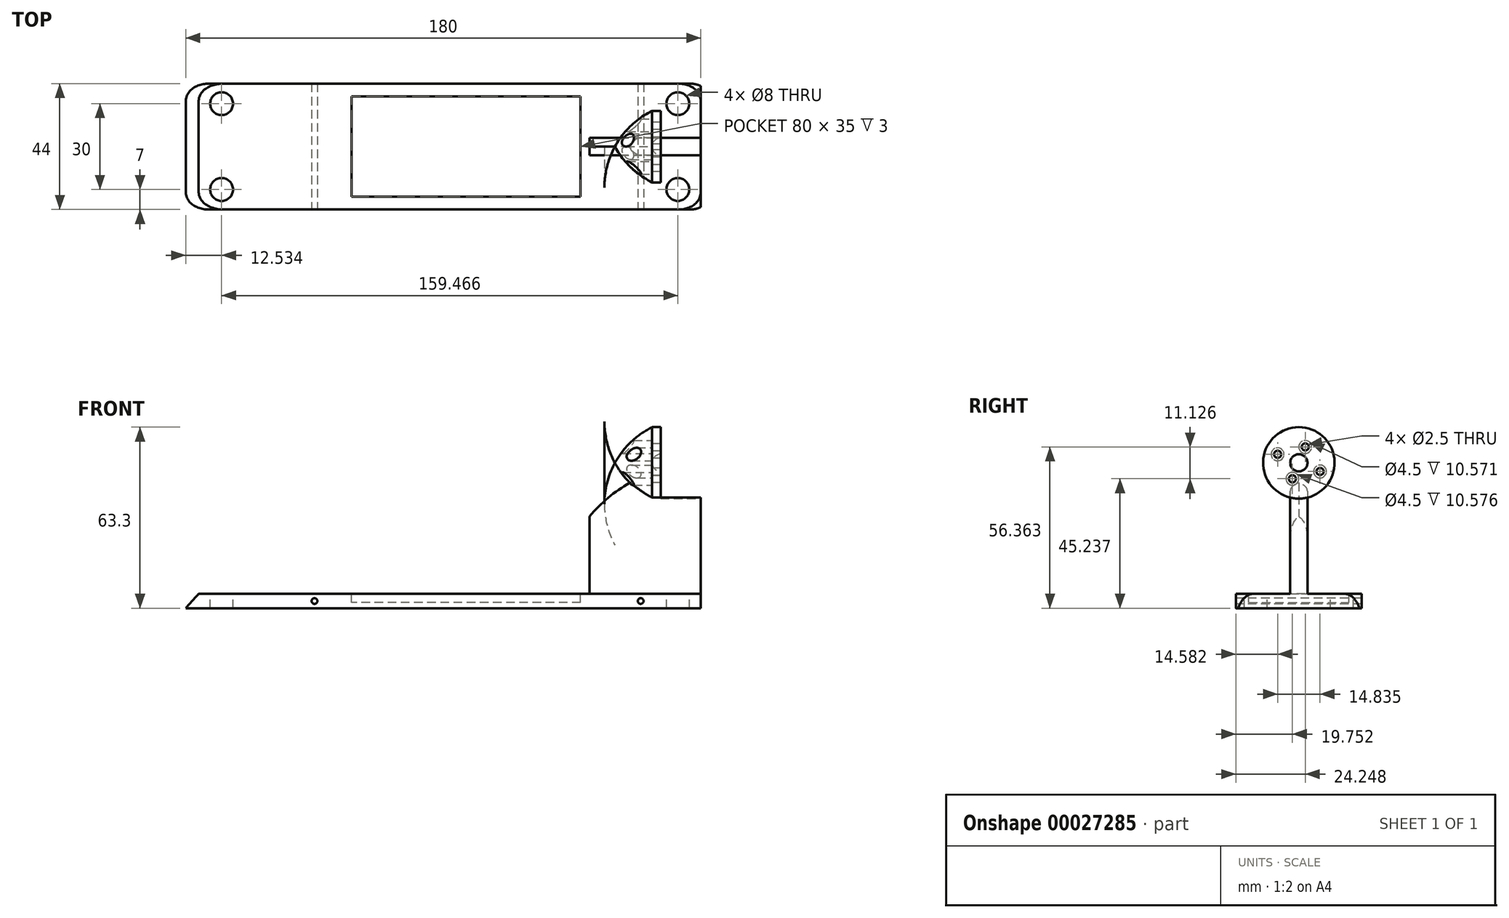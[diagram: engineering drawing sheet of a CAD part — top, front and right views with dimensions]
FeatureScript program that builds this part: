
annotation { "Feature Type Name" : "Feature", "Feature Type Description" : "" }
export const myFeature = defineFeature(function(context is Context, id is Id, definition is map)
    precondition{}
    {
        {
            var Q0;
            Q0=qCreatedBy(makeId("Top.planeOp"),FACE);
            var sketch = newSketch(context, id + "F0", { "sketchPlane" : qUnion([Q0])});
            skLineSegment(sketch, "E0.bottom", {"start": v(90, 22) * mm, "end": v(-90, 22) * mm});
            skLineSegment(sketch, "E0.top", {"start": v(90, -22) * mm, "end": v(-90, -22) * mm});
            skLineSegment(sketch, "E0.left", {"start": v(90, 22) * mm, "end": v(90, -22) * mm});
            skLineSegment(sketch, "E0.right", {"start": v(-90, 22) * mm, "end": v(-90, -22) * mm});
            skPoint(sketch, "E0.middle", {"position": v(0, 0) * mm});
            skSolve(sketch);
        }
        {
            var Q0;
            Q0 = qSketchRegion(id + "F0", true);
            extrude(context, id + "F1", {"entities" : qUnion([Q0]), "depth" : 37 * mm});
        }
        {
            var Q0;
            Q0=makeQuery(id+"F1.opExtrude","SWEPT_FACE",FACE,{"disambiguationData":[OSD([sQuery(id+"F0.wireOp",EDGE,"E0.left")])]});
            var sketch = newSketch(context, id + "F2", { "sketchPlane" : qUnion([Q0])});
            skLineSegment(sketch, "E1", {"start": v(0, 0) * mm, "end": v(0, 50.8) * mm});
            skCircle(sketch, "E2", {"center": v(0, 50.8) * mm, "radius": 11.5 * mm});
            skCircle(sketch, "E3", {"center": v(0, 50.8) * mm, "radius": 50.8 * mm, "construction": true});
            skSolve(sketch);
        }
        {
            var Q0;
            Q0=qCreatedBy(makeId("Front.planeOp"),FACE);
            var sketch = newSketch(context, id + "F3", { "sketchPlane" : qUnion([Q0])});
            skLineSegment(sketch, "E4.0", {"start": v(90, 0) * mm, "end": v(90, 50.8) * mm});
            skLineSegment(sketch, "E5.0", {"start": v(-90, 37) * mm, "end": v(-90, 0) * mm});
            skLineSegment(sketch, "E6.0", {"start": v(90, 37) * mm, "end": v(-90, 37) * mm});
            skArc(sketch, "E7", {"start": v(-10, 37) * mm, "mid": v(-54.07, 27.3) * mm, "end": v(-90, 0) * mm});
            skLineSegment(sketch, "E8", {"start": v(0, 37) * mm, "end": v(0, 0) * mm, "construction": true});
            skArc(sketch, "E9", {"start": v(90, 5) * mm, "mid": v(61.22, 28.57) * mm, "end": v(25, 37) * mm});
            skSolve(sketch);
        }
        {
            var Q0;
            Q0 = qSketchRegion(id + "F3", true);
            extrude(context, id + "F4", {"entities" : qUnion([Q0]), "operationType" : NewBodyOperationType.REMOVE, "oppositeDirection" : true, "depth" : 25 * mm, "hasSecondDirection" : true, "secondDirectionOppositeDirection" : false, "secondDirectionDepth" : 25 * mm});
        }
        {
            var Q0;
            Q0=qCreatedBy(makeId("Front.planeOp"),FACE);
            var sketch = newSketch(context, id + "F5", { "sketchPlane" : qUnion([Q0])});
            skLineSegment(sketch, "E10.top", {"start": v(48, 32) * mm, "end": v(-32, 32) * mm});
            skLineSegment(sketch, "E10.right", {"start": v(-32, 2) * mm, "end": v(-32, 32) * mm});
            skLineSegment(sketch, "E11", {"start": v(48, 32) * mm, "end": v(48, 2) * mm});
            skLineSegment(sketch, "E12", {"start": v(48, 2) * mm, "end": v(-32, 2) * mm});
            skSolve(sketch);
        }
        {
            var Q0;
            Q0 = qSketchRegion(id + "F5", true);
            extrude(context, id + "F6", {"entities" : qUnion([Q0]), "depth" : (35 / 2) * mm, "hasSecondDirection" : true, "secondDirectionOppositeDirection" : true, "secondDirectionDepth" : 17.5 * mm});
        }
        {
            var Q0;
            Q0=makeQuery(id+"F4.boolean.opBoolean","INTERSECT",EDGE,{"derivedFrom":[makeQuery(id+"F1.opExtrude","SWEPT_FACE",FACE,{"disambiguationData":[OSD([sQuery(id+"F0.wireOp",EDGE,"E0.bottom")])]}),makeQuery(id+"F4.opExtrude","SWEPT_FACE",FACE,{"disambiguationData":[OSD([sQuery(id+"F3.wireOp",EDGE,"E7")])]})]});
            var Q1;
            Q1=makeQuery(id+"F1.opExtrude","CAP_EDGE",EDGE,{"disambiguationData":[OSD([sQuery(id+"F0.wireOp",EDGE,"E0.bottom")])],"isStart":false});
            var Q2;
            Q2=makeQuery(id+"F4.boolean.opBoolean","INTERSECT",EDGE,{"derivedFrom":[makeQuery(id+"F1.opExtrude","SWEPT_FACE",FACE,{"disambiguationData":[OSD([sQuery(id+"F0.wireOp",EDGE,"E0.top")])]}),makeQuery(id+"F4.opExtrude","SWEPT_FACE",FACE,{"disambiguationData":[OSD([sQuery(id+"F3.wireOp",EDGE,"E7")])]})]});
            var Q3;
            Q3=makeQuery(id+"F4.boolean.opBoolean","INTERSECT",EDGE,{"derivedFrom":[makeQuery(id+"F1.opExtrude","SWEPT_FACE",FACE,{"disambiguationData":[OSD([sQuery(id+"F0.wireOp",EDGE,"E0.bottom")])]}),makeQuery(id+"F4.opExtrude","SWEPT_FACE",FACE,{"disambiguationData":[OSD([sQuery(id+"F3.wireOp",EDGE,"E9")])]})]});
            fillet(context, id + "F7", {"entities" : qUnion([Q0, Q1, Q2, Q3]), "radius" : 6 * mm, "tangentPropagation" : true, "allowEdgeOverflow" : false});
        }
        {
            var Q0;
            {var subQ1=sQuery(id+"F0.wireOp",EDGE,"E0.left");var subQ6=makeQuery(id+"F1.opExtrude","SWEPT_EDGE",EDGE,{"disambiguationData":[OSD([sQuery(id+"F0.wireOp",EDGE,"E0.top"),subQ1])]});Q0=makeQuery(id+"F2.imprint","IMPRINT",FACE,{"disambiguationData":[TD([[makeQuery(id+"F2.imprint","IMPRINT",EDGE,{"derivedFrom":subQ6}),1.0]])]});}
            var sketch = newSketch(context, id + "F8", { "sketchPlane" : qUnion([Q0])});
            skLineSegment(sketch, "E13.bottom", {"start": v(-3, 50.8) * mm, "end": v(3, 50.8) * mm});
            skLineSegment(sketch, "E13.top", {"start": v(-3, 0) * mm, "end": v(3, 0) * mm});
            skLineSegment(sketch, "E13.left", {"start": v(-3, 50.8) * mm, "end": v(-3, 0) * mm});
            skLineSegment(sketch, "E13.right", {"start": v(3, 50.8) * mm, "end": v(3, 0) * mm});
            skPoint(sketch, "E13.middle", {"position": v(0, 25.4) * mm});
            skLineSegment(sketch, "E14.0", {"start": v(0, 0) * mm, "end": v(0, 50.8) * mm, "construction": true});
            skSolve(sketch);
        }
        {
            var Q0;
            Q0 = qSketchRegion(id + "F8", true);
            var Q1;
            Q1=sQuery(id+"F8.wireOp",EDGE,"E13.top");
            revolve(context, id + "F9", {"operationType" : NewBodyOperationType.ADD, "entities" : qUnion([Q0]), "axis" : qUnion([Q1]), "revolveType" : RevolveType.ONE_DIRECTION, "oppositeDirection" : true, "angle" : 56 * degree});
        }
        {
            var Q0;
            Q0=makeQuery(id+"F2.imprint","IMPRINT",FACE,{"disambiguationData":[TD([[makeQuery(id+"F2.imprint","IMPRINT",EDGE,{"derivedFrom":sQuery(id+"F2.wireOp",EDGE,"E2")}),1.0]])]});
            var sketch = newSketch(context, id + "F10", { "sketchPlane" : qUnion([Q0])});
            skCircle(sketch, "E15.0", {"center": v(0, 50.8) * mm, "radius": 11.5 * mm, "construction": true});
            skCircle(sketch, "E16.0", {"center": v(0, 50.8) * mm, "radius": 12.5 * mm});
            skSolve(sketch);
        }
        {
            var Q0;
            Q0 = qSketchRegion(id + "F10", true);
            extrude(context, id + "F11", {"entities" : qUnion([Q0]), "operationType" : NewBodyOperationType.REMOVE, "oppositeDirection" : true, "depth" : 14 * mm});
        }
        {
            var Q0;
            Q0=qCreatedBy(makeId("Front.planeOp"),FACE);
            var sketch = newSketch(context, id + "F12", { "sketchPlane" : qUnion([Q0])});
            skPoint(sketch, "E17.0", {"position": v(90, 50.8) * mm});
            skLineSegment(sketch, "E18", {"start": v(90, 50.8) * mm, "end": v(60, 50.8) * mm});
            skLineSegment(sketch, "E19", {"start": v(73, 50.8) * mm, "end": v(73, 38.3) * mm, "construction": true});
            skArc(sketch, "E20", {"start": v(60, 50.8) * mm, "mid": v(65.54, 43.55) * mm, "end": v(73, 38.3) * mm});
            skLineSegment(sketch, "E21.0", {"start": v(76, 38.3) * mm, "end": v(76, 50.8) * mm});
            skPoint(sketch, "E22.orphan", {"position": v(76, 48.83) * mm});
            skLineSegment(sketch, "E23", {"start": v(73, 38.3) * mm, "end": v(76, 38.3) * mm});
            skPoint(sketch, "E24.orphan", {"position": v(76, 38.67) * mm});
            skSolve(sketch);
        }
        {
            var Q0;
            Q0 = qSketchRegion(id + "F12", true);
            var Q1;
            Q1=sQuery(id+"F12.wireOp",EDGE,"E18");
            revolve(context, id + "F13", {"operationType" : NewBodyOperationType.ADD, "entities" : qUnion([Q0]), "axis" : qUnion([Q1]), "revolveType" : RevolveType.FULL});
        }
        {
            var Q0;
            Q0=makeQuery(id+"F13.boolean.opBoolean","MERGE",FACE,{"derivedFrom":[makeQuery(id+"F11.boolean.opBoolean","COPY",FACE,{"derivedFrom":makeQuery(id+"F11.opExtrude","CAP_FACE",FACE,{"disambiguationData":[OSD([sQuery(id+"F10.wireOp",EDGE,"E16.0")])],"isStart":false})}),makeQuery(id+"F13.opRevolve","SWEPT_FACE",FACE,{"disambiguationData":[OSD([sQuery(id+"F12.wireOp",EDGE,"E21.0")])]})]});
            var sketch = newSketch(context, id + "F14", { "sketchPlane" : qUnion([Q0])});
            skLineSegment(sketch, "E25", {"start": v(7.42, 47.8) * mm, "end": v(-7.42, 53.8) * mm, "construction": true});
            skLineSegment(sketch, "E26", {"start": v(2.25, 56.36) * mm, "end": v(-2.25, 45.24) * mm, "construction": true});
            skCircle(sketch, "E27", {"center": v(-7.42, 53.8) * mm, "radius": 1.25 * mm});
            skCircle(sketch, "E28", {"center": v(2.25, 56.36) * mm, "radius": 1.25 * mm});
            skCircle(sketch, "E29", {"center": v(-2.25, 45.24) * mm, "radius": 1.25 * mm});
            skCircle(sketch, "E30", {"center": v(7.42, 47.8) * mm, "radius": 1.25 * mm});
            skSolve(sketch);
        }
        {
            var Q0;
            Q0 = qSketchRegion(id + "F14", true);
            extrude(context, id + "F15", {"entities" : qUnion([Q0]), "operationType" : NewBodyOperationType.REMOVE, "endBound" : BoundingType.THROUGH_ALL, "oppositeDirection" : true, "depth" : 25 * mm});
        }
        {
            var Q0;
            Q0=makeQuery(id+"F13.boolean.opBoolean","MERGE",FACE,{"derivedFrom":[makeQuery(id+"F11.boolean.opBoolean","COPY",FACE,{"derivedFrom":makeQuery(id+"F11.opExtrude","CAP_FACE",FACE,{"disambiguationData":[OSD([sQuery(id+"F10.wireOp",EDGE,"E16.0")])],"isStart":false})}),makeQuery(id+"F13.opRevolve","SWEPT_FACE",FACE,{"disambiguationData":[OSD([sQuery(id+"F12.wireOp",EDGE,"E21.0")])]})]});
            var sketch = newSketch(context, id + "F16", { "sketchPlane" : qUnion([Q0])});
            skCircle(sketch, "E31", {"center": v(0, 50.8) * mm, "radius": 3 * mm});
            skSolve(sketch);
        }
        {
            var Q0;
            Q0 = qSketchRegion(id + "F16", true);
            extrude(context, id + "F17", {"entities" : qUnion([Q0]), "operationType" : NewBodyOperationType.REMOVE, "oppositeDirection" : true, "depth" : 3 * mm});
        }
        {
            var Q0;
            Q0=makeQuery(id+"F17.boolean.opBoolean","COPY",EDGE,{"derivedFrom":makeQuery(id+"F17.opExtrude","CAP_EDGE",EDGE,{"disambiguationData":[OSD([sQuery(id+"F16.wireOp",EDGE,"E31")])],"isStart":false})});
            fillet(context, id + "F18", {"entities" : qUnion([Q0]), "radius" : 3 * mm, "tangentPropagation" : true, "allowEdgeOverflow" : false});
        }
        {
            var Q0;
            Q0=makeQuery(id+"F13.boolean.opBoolean","MERGE",FACE,{"derivedFrom":[makeQuery(id+"F11.boolean.opBoolean","COPY",FACE,{"derivedFrom":makeQuery(id+"F11.opExtrude","CAP_FACE",FACE,{"disambiguationData":[OSD([sQuery(id+"F10.wireOp",EDGE,"E16.0")])],"isStart":false})}),makeQuery(id+"F13.opRevolve","SWEPT_FACE",FACE,{"disambiguationData":[OSD([sQuery(id+"F12.wireOp",EDGE,"E21.0")])]})]});
            var sketch = newSketch(context, id + "F19", { "sketchPlane" : qUnion([Q0])});
            skCircle(sketch, "E32", {"center": v(-7.42, 53.8) * mm, "radius": 2.25 * mm});
            skCircle(sketch, "E33", {"center": v(2.25, 56.36) * mm, "radius": 2.25 * mm});
            skCircle(sketch, "E34", {"center": v(7.42, 47.8) * mm, "radius": 2.25 * mm});
            skCircle(sketch, "E35", {"center": v(-2.25, 45.24) * mm, "radius": 2.25 * mm});
            skSolve(sketch);
        }
        {
            var Q0;
            Q0 = qSketchRegion(id + "F19", true);
            extrude(context, id + "F20", {"entities" : qUnion([Q0]), "operationType" : NewBodyOperationType.REMOVE, "endBound" : BoundingType.THROUGH_ALL, "oppositeDirection" : true, "depth" : 6.3 * mm, "hasSecondDirection" : true, "secondDirectionOppositeDirection" : true, "secondDirectionDepth" : 3 * mm});
        }
        {
            var Q0;
            {var subQ1=sQuery(id+"F0.wireOp",EDGE,"E0.left");var subQ6=makeQuery(id+"F1.opExtrude","SWEPT_EDGE",EDGE,{"disambiguationData":[OSD([sQuery(id+"F0.wireOp",EDGE,"E0.bottom"),subQ1])]});Q0=makeQuery(id+"F2.imprint","IMPRINT",FACE,{"disambiguationData":[TD([[makeQuery(id+"F2.imprint","IMPRINT",EDGE,{"derivedFrom":subQ6}),-1.0]])]});}
            var sketch = newSketch(context, id + "F21", { "sketchPlane" : qUnion([Q0])});
            skLineSegment(sketch, "E36", {"start": v(-28, 5) * mm, "end": v(-3, 5) * mm});
            skLineSegment(sketch, "E37.0", {"start": v(-3, 38.67) * mm, "end": v(-3, 5) * mm});
            skLineSegment(sketch, "E37.1", {"start": v(3, 38.67) * mm, "end": v(3, 5) * mm});
            skLineSegment(sketch, "E38.trimOffspring", {"start": v(3, 5) * mm, "end": v(28, 5) * mm});
            skLineSegment(sketch, "E39", {"start": v(-28, 5) * mm, "end": v(-28, 38.67) * mm});
            skLineSegment(sketch, "E40", {"start": v(-28, 38.67) * mm, "end": v(-3, 38.67) * mm});
            skLineSegment(sketch, "E41", {"start": v(28, 5) * mm, "end": v(28, 38.67) * mm});
            skLineSegment(sketch, "E42", {"start": v(28, 38.67) * mm, "end": v(3, 38.67) * mm});
            skSolve(sketch);
        }
        {
            var Q0;
            Q0 = qSketchRegion(id + "F21", true);
            extrude(context, id + "F22", {"entities" : qUnion([Q0]), "operationType" : NewBodyOperationType.REMOVE, "endBound" : BoundingType.THROUGH_ALL, "oppositeDirection" : true, "depth" : 25 * mm});
        }
        {
            var Q0;
            Q0=makeQuery(id+"F22.boolean.opBoolean","MERGE",FACE,{"derivedFrom":[makeQuery(id+"F9.opRevolve","SWEPT_FACE",FACE,{"disambiguationData":[OSD([sQuery(id+"F8.wireOp",EDGE,"E13.left")])]}),makeQuery(id+"F22.opExtrude","SWEPT_FACE",FACE,{"disambiguationData":[OSD([sQuery(id+"F21.wireOp",EDGE,"E37.0")])]})]});
            var sketch = newSketch(context, id + "F23", { "sketchPlane" : qUnion([Q0])});
            skLineSegment(sketch, "E43", {"start": v(51.14, 32.72) * mm, "end": v(51.14, 5) * mm});
            skArc(sketch, "E44.0", {"start": v(-85.47, 5) * mm, "mid": v(-50.99, 28.67) * mm, "end": v(-10, 37) * mm});
            skLineSegment(sketch, "E45.0", {"start": v(-10, 37) * mm, "end": v(25, 37) * mm});
            skArc(sketch, "E46.0", {"start": v(25, 37) * mm, "mid": v(38.25, 35.92) * mm, "end": v(51.14, 32.72) * mm});
            skLineSegment(sketch, "E47.0", {"start": v(-76.87, 5) * mm, "end": v(82.24, 5) * mm});
            skFitSpline(sketch, "E48.0", {"points": [v(-85.47, 5) * mm, v(-82.6, 5) * mm, v(-79.73, 5) * mm, v(-76.87, 5) * mm]});
            skSolve(sketch);
        }
        {
            var Q0;
            Q0 = qSketchRegion(id + "F23", true);
            extrude(context, id + "F24", {"entities" : qUnion([Q0]), "operationType" : NewBodyOperationType.REMOVE, "oppositeDirection" : true, "depth" : 25 * mm});
        }
        {
            var Q0;
            Q0=makeQuery(id+"F24.boolean.opBoolean","MERGE",FACE,{"derivedFrom":[makeQuery(id+"F22.boolean.opBoolean","COPY",FACE,{"derivedFrom":makeQuery(id+"F22.opExtrude","SWEPT_FACE",FACE,{"disambiguationData":[OSD([sQuery(id+"F21.wireOp",EDGE,"E36")])]})}),makeQuery(id+"F22.boolean.opBoolean","COPY",FACE,{"derivedFrom":makeQuery(id+"F22.opExtrude","SWEPT_FACE",FACE,{"disambiguationData":[OSD([sQuery(id+"F21.wireOp",EDGE,"E38.trimOffspring")])]})}),makeQuery(id+"F24.opExtrude","SWEPT_FACE",FACE,{"disambiguationData":[OSD([sQuery(id+"F23.wireOp",EDGE,"E47.0"),sQuery(id+"F23.wireOp",EDGE,"E48.0")])]})]});
            var sketch = newSketch(context, id + "F25", { "sketchPlane" : qUnion([Q0])});
            skLineSegment(sketch, "E49.0", {"start": v(48, 17.5) * mm, "end": v(-32, 17.5) * mm});
            skLineSegment(sketch, "E50.0", {"start": v(-32, -17.5) * mm, "end": v(-32, 17.5) * mm});
            skLineSegment(sketch, "E51.0", {"start": v(48, -17.5) * mm, "end": v(-32, -17.5) * mm});
            skLineSegment(sketch, "E52.0", {"start": v(48, -17.5) * mm, "end": v(48, 17.5) * mm});
            skSolve(sketch);
        }
        {
            var Q0;
            Q0 = qSketchRegion(id + "F25", true);
            extrude(context, id + "F26", {"entities" : qUnion([Q0]), "operationType" : NewBodyOperationType.REMOVE, "oppositeDirection" : true, "depth" : 3 * mm});
        }
        {
            var Q0;
            Q0=qCreatedBy(makeId("Front.planeOp"),FACE);
            var sketch = newSketch(context, id + "F27", { "sketchPlane" : qUnion([Q0])});
            skCircle(sketch, "E53", {"center": v(-45, 2.5) * mm, "radius": 1 * mm});
            skCircle(sketch, "E54", {"center": v(69, 2.5) * mm, "radius": 1 * mm});
            skSolve(sketch);
        }
        {
            var Q0;
            Q0 = qSketchRegion(id + "F27", true);
            extrude(context, id + "F28", {"entities" : qUnion([Q0]), "operationType" : NewBodyOperationType.REMOVE, "oppositeDirection" : true, "depth" : 25 * mm, "hasSecondDirection" : true, "secondDirectionOppositeDirection" : false, "secondDirectionDepth" : 25 * mm});
        }
        {
            var Q0;
            Q0=makeQuery(id+"F24.boolean.opBoolean","MERGE",FACE,{"derivedFrom":[makeQuery(id+"F22.boolean.opBoolean","COPY",FACE,{"derivedFrom":makeQuery(id+"F22.opExtrude","SWEPT_FACE",FACE,{"disambiguationData":[OSD([sQuery(id+"F21.wireOp",EDGE,"E36")])]})}),makeQuery(id+"F22.boolean.opBoolean","COPY",FACE,{"derivedFrom":makeQuery(id+"F22.opExtrude","SWEPT_FACE",FACE,{"disambiguationData":[OSD([sQuery(id+"F21.wireOp",EDGE,"E38.trimOffspring")])]})}),makeQuery(id+"F24.opExtrude","SWEPT_FACE",FACE,{"disambiguationData":[OSD([sQuery(id+"F23.wireOp",EDGE,"E47.0"),sQuery(id+"F23.wireOp",EDGE,"E48.0")])]})]});
            var sketch = newSketch(context, id + "F29", { "sketchPlane" : qUnion([Q0])});
            skCircle(sketch, "E55", {"center": v(-77.47, -15) * mm, "radius": 4 * mm});
            skCircle(sketch, "E56", {"center": v(82, -15) * mm, "radius": 4 * mm});
            skCircle(sketch, "E57.MirrorC", {"center": v(-77.47, 15) * mm, "radius": 4 * mm});
            skCircle(sketch, "E58.MirrorC", {"center": v(82, 15) * mm, "radius": 4 * mm});
            skSolve(sketch);
        }
        {
            var Q0;
            Q0 = qSketchRegion(id + "F29", true);
            extrude(context, id + "F30", {"entities" : qUnion([Q0]), "operationType" : NewBodyOperationType.REMOVE, "oppositeDirection" : true, "depth" : 25 * mm});
        }
        {
            var Q0;
            Q0=makeQuery(id+"F9.opRevolve","SWEPT_EDGE",EDGE,{"disambiguationData":[OSD([sQuery(id+"F8.wireOp",EDGE,"E13.bottom"),sQuery(id+"F8.wireOp",EDGE,"E13.right")])]});
            var Q1;
            Q1=makeQuery(id+"F9.opRevolve","SWEPT_EDGE",EDGE,{"disambiguationData":[OSD([sQuery(id+"F8.wireOp",EDGE,"E13.bottom"),sQuery(id+"F8.wireOp",EDGE,"E13.left")])]});
            fillet(context, id + "F31", {"entities" : qUnion([Q0, Q1]), "radius" : 5 * mm, "tangentPropagation" : true, "allowEdgeOverflow" : false});
        }
    });
